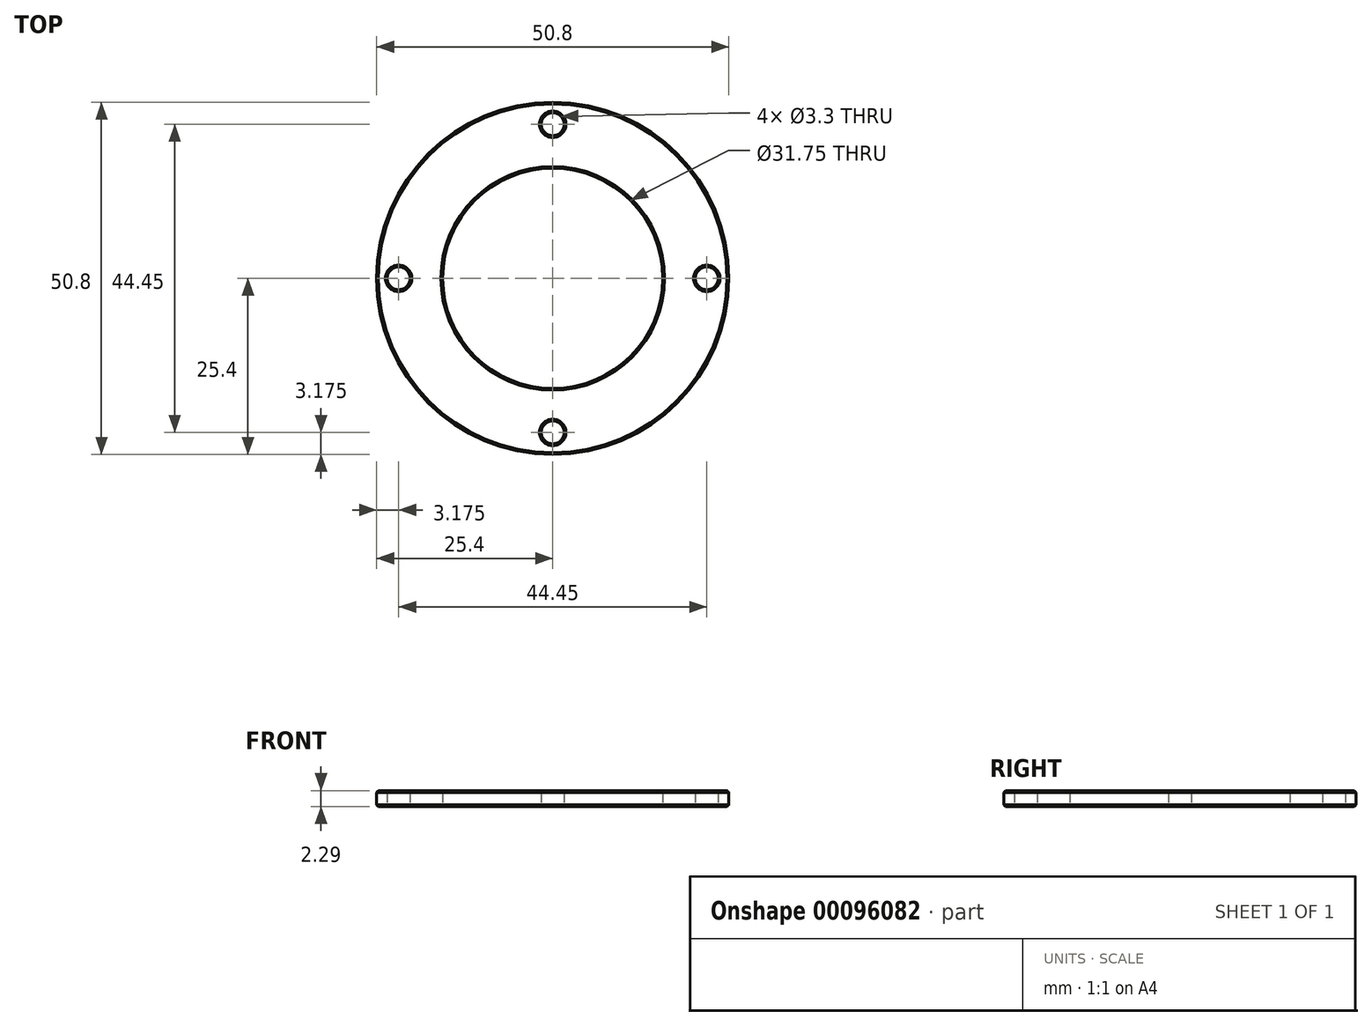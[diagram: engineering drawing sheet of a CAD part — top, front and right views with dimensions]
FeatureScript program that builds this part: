
annotation { "Feature Type Name" : "Feature", "Feature Type Description" : "" }
export const myFeature = defineFeature(function(context is Context, id is Id, definition is map)
    precondition{}
    {
        {
            var Q0;
            Q0=qCreatedBy(makeId("Top.planeOp"),FACE);
            var sketch = newSketch(context, id + "F0", { "sketchPlane" : qUnion([Q0])});
            skCircle(sketch, "E0", {"center": v(0, 0) * mm, "radius": 25.4 * mm});
            skCircle(sketch, "E1", {"center": v(0, 0) * mm, "radius": 15.88 * mm});
            skCircle(sketch, "E2", {"center": v(0, 0) * mm, "radius": 22.23 * mm});
            skCircle(sketch, "E3", {"center": v(0, 22.23) * mm, "radius": 1.65 * mm});
            skCircle(sketch, "E4.1.0", {"center": v(-22.23, 0) * mm, "radius": 1.65 * mm});
            skCircle(sketch, "E4.2.0", {"center": v(0, -22.23) * mm, "radius": 1.65 * mm});
            skCircle(sketch, "E4.3.0", {"center": v(22.23, 0) * mm, "radius": 1.65 * mm});
            skSolve(sketch);
        }
        {
            var Q0;
            Q0=makeQuery(id+"F0.imprint","IMPRINT",FACE,{"disambiguationData":[TD([[makeQuery(id+"F0.imprint","IMPRINT",EDGE,{"derivedFrom":sQuery(id+"F0.wireOp",EDGE,"E0")}),1.0]])]});
            var Q1;
            Q1=makeQuery(id+"F0.imprint","IMPRINT",FACE,{"disambiguationData":[TD([[makeQuery(id+"F0.imprint","IMPRINT",EDGE,{"derivedFrom":sQuery(id+"F0.wireOp",EDGE,"E1")}),-1.0]])]});
            extrude(context, id + "F1", {"entities" : qUnion([Q0, Q1]), "depth" : 2.3 * mm});
        }
        {
            var Q0;
            Q0=makeQuery(id+"F1.opExtrude","CAP_EDGE",EDGE,{"disambiguationData":[OSD([sQuery(id+"F0.wireOp",EDGE,"E0")])],"isStart":true});
            var Q1;
            Q1=makeQuery(id+"F1.opExtrude","CAP_EDGE",EDGE,{"disambiguationData":[OSD([sQuery(id+"F0.wireOp",EDGE,"E0")])],"isStart":false});
            var Q2;
            Q2=makeQuery(id+"F1.opExtrude","CAP_EDGE",EDGE,{"disambiguationData":[OSD([sQuery(id+"F0.wireOp",EDGE,"E1")])],"isStart":false});
            var Q3;
            Q3=makeQuery(id+"F1.opExtrude","CAP_EDGE",EDGE,{"disambiguationData":[OSD([sQuery(id+"F0.wireOp",EDGE,"E1")])],"isStart":true});
            var Q4;
            Q4=makeQuery(id+"F1.opExtrude","SWEPT_FACE",FACE,{"disambiguationData":[OSD([sQuery(id+"F0.wireOp",EDGE,"E4.1.0")])]});
            var Q5;
            Q5=makeQuery(id+"F1.opExtrude","SWEPT_FACE",FACE,{"disambiguationData":[OSD([sQuery(id+"F0.wireOp",EDGE,"E4.2.0")])]});
            var Q6;
            Q6=makeQuery(id+"F1.opExtrude","SWEPT_FACE",FACE,{"disambiguationData":[OSD([sQuery(id+"F0.wireOp",EDGE,"E4.3.0")])]});
            var Q7;
            Q7=makeQuery(id+"F1.opExtrude","SWEPT_FACE",FACE,{"disambiguationData":[OSD([sQuery(id+"F0.wireOp",EDGE,"E3")])]});
            chamfer(context, id + "F2", {"entities" : qUnion([Q0, Q1, Q2, Q3, Q4, Q5, Q6, Q7]), "width" : 0.25 * mm, "tangentPropagation" : true});
        }
    });
